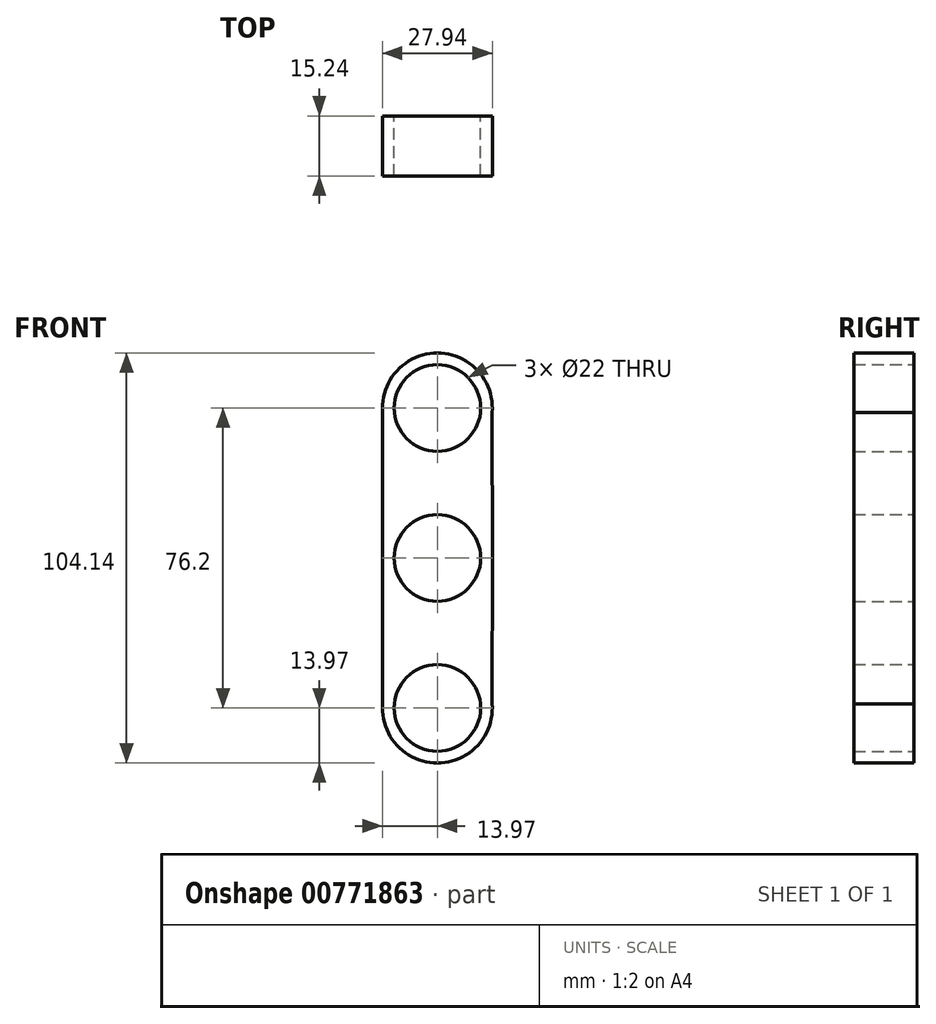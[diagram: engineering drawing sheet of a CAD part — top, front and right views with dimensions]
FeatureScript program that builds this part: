
annotation { "Feature Type Name" : "Feature", "Feature Type Description" : "" }
export const myFeature = defineFeature(function(context is Context, id is Id, definition is map)
    precondition{}
    {
        {
            var Q0;
            Q0=qCreatedBy(makeId("Front.planeOp"),FACE);
            var sketch = newSketch(context, id + "F0", { "sketchPlane" : qUnion([Q0])});
            skLineSegment(sketch, "E0", {"start": v(0, 0) * mm, "end": v(0, 38.1) * mm});
            skCircle(sketch, "E1", {"center": v(0, 38.1) * mm, "radius": 11 * mm});
            skCircle(sketch, "E2", {"center": v(0, 38.1) * mm, "radius": 13.97 * mm});
            skCircle(sketch, "E3", {"center": v(0, 0) * mm, "radius": 11 * mm});
            skLineSegment(sketch, "E4", {"start": v(0, 0) * mm, "end": v(0, -38.1) * mm});
            skCircle(sketch, "E5", {"center": v(0, -38.1) * mm, "radius": 11 * mm});
            skCircle(sketch, "E6", {"center": v(0, -38.1) * mm, "radius": 13.97 * mm});
            skLineSegment(sketch, "E7", {"start": v(0, 0) * mm, "end": v(13.97, 0) * mm});
            skLineSegment(sketch, "E8", {"start": v(0, 0) * mm, "end": v(-13.97, 0) * mm});
            skLineSegment(sketch, "E9", {"start": v(13.93, 37.01) * mm, "end": v(13.97, 0) * mm});
            skLineSegment(sketch, "E10", {"start": v(-13.93, 37.01) * mm, "end": v(-13.97, 0) * mm});
            skLineSegment(sketch, "E11", {"start": v(-13.97, 0) * mm, "end": v(-13.93, -37.01) * mm});
            skLineSegment(sketch, "E12", {"start": v(13.97, 0) * mm, "end": v(13.93, -37.01) * mm});
            skSolve(sketch);
        }
        {
            var Q0;
            Q0 = qSketchRegion(id + "F0", true);
            extrude(context, id + "F1", {"entities" : qUnion([Q0]), "depth" : 15.24 * mm, "offsetDistance" : 25.4 * mm});
        }
    });
